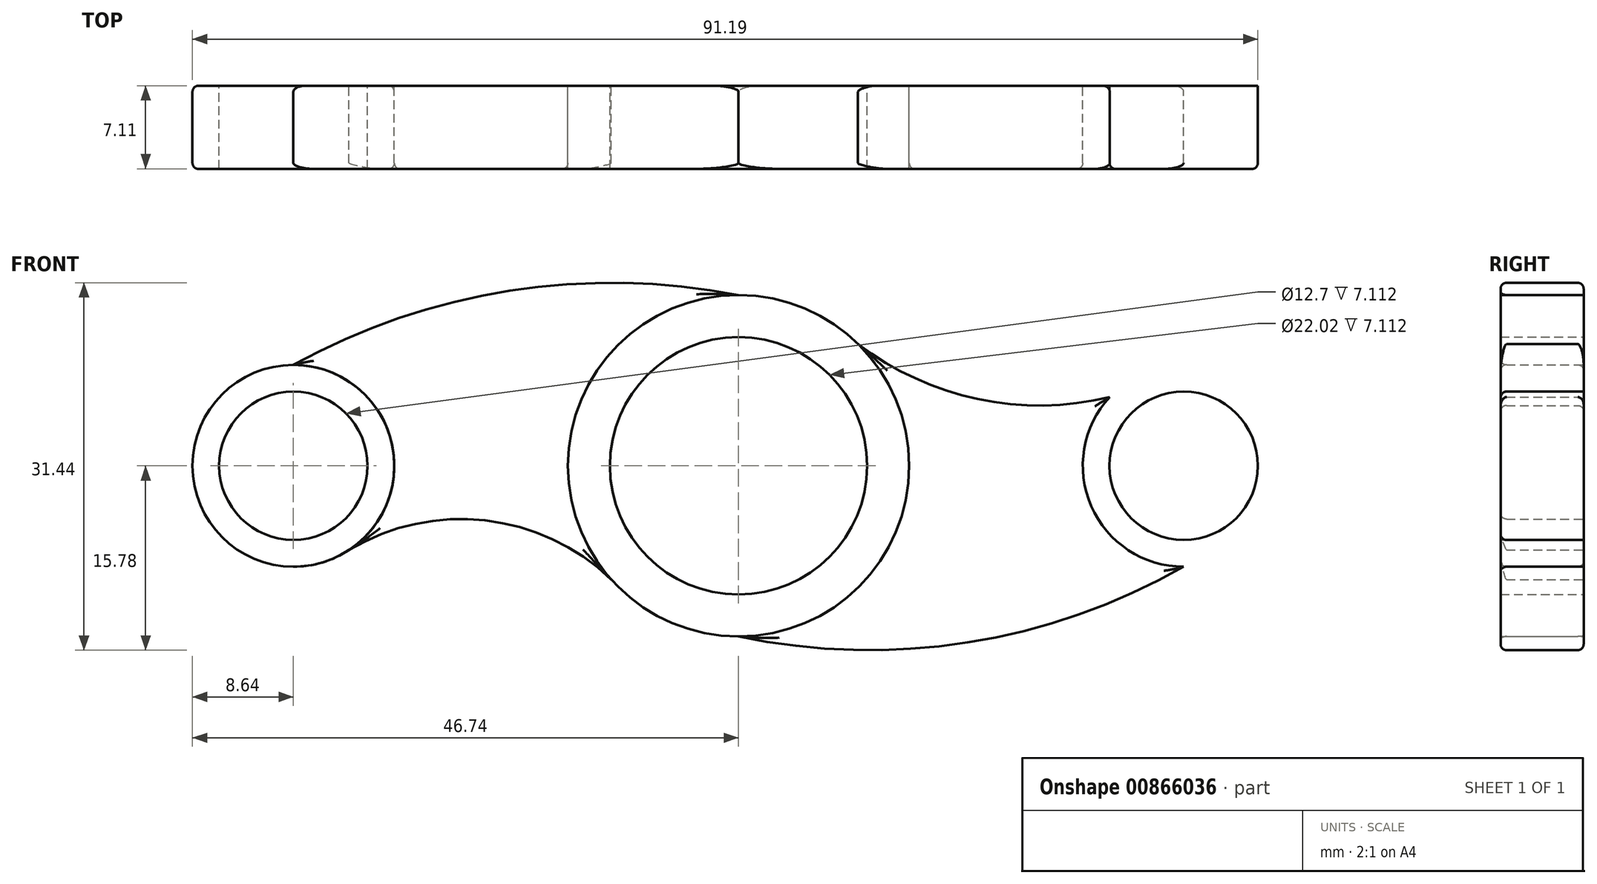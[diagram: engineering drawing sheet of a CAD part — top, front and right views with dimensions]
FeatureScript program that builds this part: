
annotation { "Feature Type Name" : "Feature", "Feature Type Description" : "" }
export const myFeature = defineFeature(function(context is Context, id is Id, definition is map)
    precondition{}
    {
        {
            var Q0;
            Q0=qCreatedBy(makeId("Front.planeOp"),FACE);
            var sketch = newSketch(context, id + "F0", { "sketchPlane" : qUnion([Q0])});
            skCircle(sketch, "E0", {"center": v(0, 0) * mm, "radius": 11.01 * mm});
            skCircle(sketch, "E1", {"center": v(0, 0) * mm, "radius": 14.6 * mm});
            skLineSegment(sketch, "E2", {"start": v(-38.1, 22.23) * mm, "end": v(-38.1, -24.16) * mm, "construction": true});
            skCircle(sketch, "E3", {"center": v(-38.1, 0) * mm, "radius": 6.35 * mm});
            skCircle(sketch, "E4", {"center": v(-38.1, 0) * mm, "radius": 8.64 * mm});
            skArc(sketch, "E5", {"start": v(0, 14.6) * mm, "mid": v(-19.58, 14.98) * mm, "end": v(-38.1, 8.64) * mm});
            skArc(sketch, "E6", {"start": v(-10.89, -9.73) * mm, "mid": v(-21.69, -4.68) * mm, "end": v(-33.34, -7.2) * mm});
            skCircle(sketch, "E7.MirrorC", {"center": v(38.1, 0) * mm, "radius": 8.64 * mm});
            skCircle(sketch, "E8.MirrorC", {"center": v(38.1, 0) * mm, "radius": 6.35 * mm});
            skArc(sketch, "E9", {"start": v(10.22, 10.43) * mm, "mid": v(20.48, 5.71) * mm, "end": v(31.77, 5.88) * mm});
            skLineSegment(sketch, "E10.MirrorCS", {"start": v(38.1, 22.23) * mm, "end": v(38.1, -24.16) * mm, "construction": true});
            skArc(sketch, "E11", {"start": v(0, -14.6) * mm, "mid": v(19.6, -15.12) * mm, "end": v(38.1, -8.64) * mm});
            skCircle(sketch, "E12", {"center": v(-40.18, -29.28) * mm, "radius": 5.38 * mm});
            skCircle(sketch, "E13", {"center": v(-40.18, -29.28) * mm, "radius": 8.64 * mm});
            skArc(sketch, "E14", {"start": v(-78.28, -43.89) * mm, "mid": v(-58.7, -44.26) * mm, "end": v(-40.18, -37.92) * mm});
            skArc(sketch, "E15.MirrorCS", {"start": v(-67.39, -19.55) * mm, "mid": v(-56.6, -24.6) * mm, "end": v(-44.94, -22.08) * mm});
            skSolve(sketch);
        }
        {
            var Q0;
            Q0=makeQuery(id+"F0.imprint","IMPRINT",FACE,{"disambiguationData":[TD([[makeQuery(id+"F0.imprint","IMPRINT",EDGE,{"derivedFrom":sQuery(id+"F0.wireOp",EDGE,"E8.MirrorC")}),1.0]])]});
            var Q1;
            Q1=makeQuery(id+"F0.imprint","IMPRINT",FACE,{"disambiguationData":[TD([[makeQuery(id+"F0.imprint","IMPRINT",EDGE,{"derivedFrom":sQuery(id+"F0.wireOp",EDGE,"E0")}),-1.0]])]});
            var Q2;
            Q2=makeQuery(id+"F0.imprint","IMPRINT",FACE,{"disambiguationData":[TD([[makeQuery(id+"F0.imprint","IMPRINT",EDGE,{"derivedFrom":sQuery(id+"F0.wireOp",EDGE,"E3")}),-1.0]])]});
            extrude(context, id + "F1", {"entities" : qUnion([Q0, Q1, Q2]), "depth" : 7.11 * mm, "offsetDistance" : 25.4 * mm});
        }
        {
            var Q0;
            {var subQ0=sQuery(id+"F0.wireOp",EDGE,"E5");Q0=makeQuery(id+"F0.imprint","IMPRINT",FACE,{"disambiguationData":[TD([[makeQuery(id+"F0.imprint","IMPRINT",EDGE,{"derivedFrom":subQ0}),1.0]])]});}
            var Q1;
            {var subQ0=sQuery(id+"F0.wireOp",EDGE,"E9");Q1=makeQuery(id+"F0.imprint","IMPRINT",FACE,{"disambiguationData":[TD([[makeQuery(id+"F0.imprint","IMPRINT",EDGE,{"derivedFrom":subQ0}),-1.0]])]});}
            extrude(context, id + "F2", {"entities" : qUnion([Q0, Q1]), "depth" : 7.11 * mm, "offsetDistance" : 25.4 * mm});
        }
        {
            var Q0;
            Q0=makeQuery(id+"F1.opExtrude","CAP_EDGE",EDGE,{"disambiguationData":[OSD([sQuery(id+"F0.wireOp",EDGE,"E4")])],"isStart":false});
            var Q1;
            Q1=makeQuery(id+"F2.opExtrude","CAP_FACE",FACE,{"disambiguationData":[OSD([sQuery(id+"F0.wireOp",EDGE,"E4"),sQuery(id+"F0.wireOp",EDGE,"E5"),sQuery(id+"F0.wireOp",EDGE,"E6"),sQuery(id+"F0.wireOp",EDGE,"E1")])],"isStart":false});
            var Q2;
            Q2=makeQuery(id+"F1.opExtrude","CAP_EDGE",EDGE,{"disambiguationData":[OSD([sQuery(id+"F0.wireOp",EDGE,"E1")])],"isStart":false});
            var Q3;
            Q3=makeQuery(id+"F2.opExtrude","CAP_FACE",FACE,{"disambiguationData":[OSD([sQuery(id+"F0.wireOp",EDGE,"E7.MirrorC"),sQuery(id+"F0.wireOp",EDGE,"E1"),sQuery(id+"F0.wireOp",EDGE,"E9"),sQuery(id+"F0.wireOp",EDGE,"E11")])],"isStart":false});
            var Q4;
            Q4=makeQuery(id+"F1.opExtrude","CAP_FACE",FACE,{"disambiguationData":[OSD([sQuery(id+"F0.wireOp",EDGE,"E7.MirrorC"),sQuery(id+"F0.wireOp",EDGE,"E8.MirrorC")])],"isStart":false});
            var Q5;
            Q5=makeQuery(id+"F2.opExtrude","CAP_EDGE",EDGE,{"disambiguationData":[OSD([sQuery(id+"F0.wireOp",EDGE,"E11")])],"isStart":true});
            var Q6;
            Q6=makeQuery(id+"F2.opExtrude","CAP_EDGE",EDGE,{"disambiguationData":[OSD([sQuery(id+"F0.wireOp",EDGE,"E9")])],"isStart":true});
            var Q7;
            Q7=makeQuery(id+"F1.opExtrude","CAP_EDGE",EDGE,{"disambiguationData":[OSD([sQuery(id+"F0.wireOp",EDGE,"E7.MirrorC")])],"isStart":true});
            var Q8;
            Q8=makeQuery(id+"F1.opExtrude","CAP_EDGE",EDGE,{"disambiguationData":[OSD([sQuery(id+"F0.wireOp",EDGE,"E1")])],"isStart":true});
            var Q9;
            Q9=makeQuery(id+"F2.opExtrude","CAP_EDGE",EDGE,{"disambiguationData":[OSD([sQuery(id+"F0.wireOp",EDGE,"E6")])],"isStart":true});
            var Q10;
            Q10=makeQuery(id+"F2.opExtrude","CAP_EDGE",EDGE,{"disambiguationData":[OSD([sQuery(id+"F0.wireOp",EDGE,"E5")])],"isStart":true});
            var Q11;
            Q11=makeQuery(id+"F1.opExtrude","CAP_EDGE",EDGE,{"disambiguationData":[OSD([sQuery(id+"F0.wireOp",EDGE,"E4")])],"isStart":true});
            var Q12;
            Q12=makeQuery(id+"F2.opExtrude","CAP_EDGE",EDGE,{"disambiguationData":[OSD([sQuery(id+"F0.wireOp",EDGE,"E7.MirrorC")])],"isStart":false});
            var Q13;
            Q13=makeQuery(id+"F1.opExtrude","CAP_EDGE",EDGE,{"disambiguationData":[OSD([sQuery(id+"F0.wireOp",EDGE,"E7.MirrorC")])],"isStart":false});
            fillet(context, id + "F3", {"entities" : qUnion([Q0, Q1, Q2, Q3, Q4, Q5, Q6, Q7, Q8, Q9, Q10, Q11, Q12, Q13]), "radius" : 0.5 * mm, "tangentPropagation" : true, "allowEdgeOverflow" : false});
        }
    });
